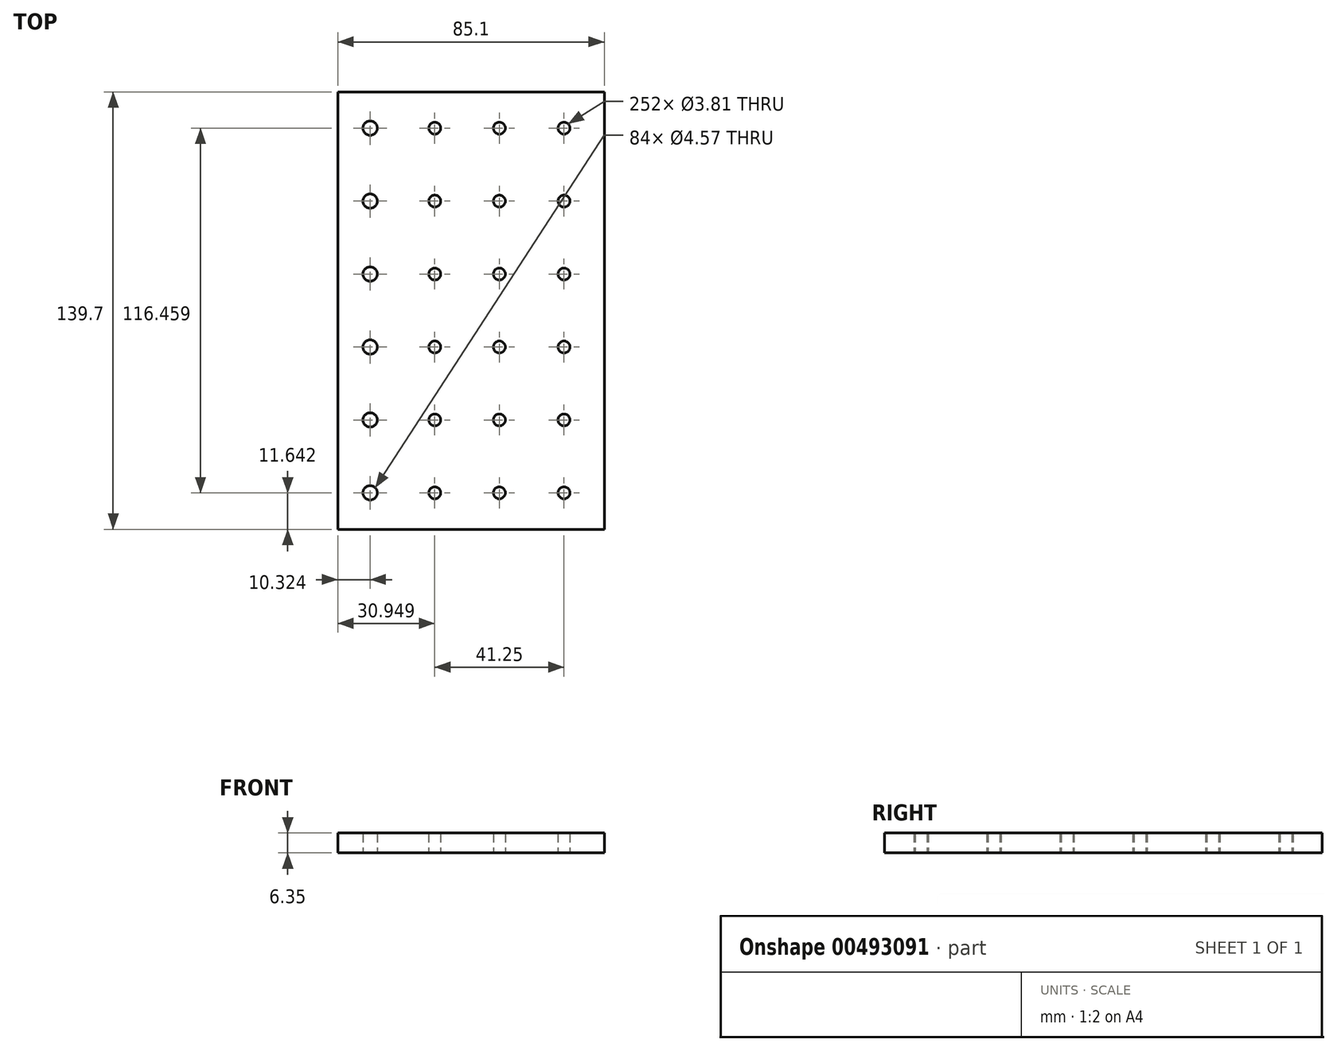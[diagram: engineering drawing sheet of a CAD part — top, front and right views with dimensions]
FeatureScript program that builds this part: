
annotation { "Feature Type Name" : "Feature", "Feature Type Description" : "" }
export const myFeature = defineFeature(function(context is Context, id is Id, definition is map)
    precondition{}
    {
        {
            var Q0;
            Q0=qCreatedBy(makeId("Top.planeOp"),FACE);
            var sketch = newSketch(context, id + "F0", { "sketchPlane" : qUnion([Q0])});
            skLineSegment(sketch, "E0.bottom", {"start": v(-42.54, 69.85) * mm, "end": v(42.55, 69.85) * mm});
            skLineSegment(sketch, "E0.top", {"start": v(-42.55, -69.85) * mm, "end": v(42.55, -69.85) * mm});
            skLineSegment(sketch, "E0.left", {"start": v(-42.54, 69.85) * mm, "end": v(-42.55, -69.85) * mm});
            skLineSegment(sketch, "E0.right", {"start": v(42.55, 69.85) * mm, "end": v(42.55, -69.85) * mm});
            skPoint(sketch, "E0.middle", {"position": v(0, 0) * mm});
            skSolve(sketch);
        }
        {
            var Q0;
            Q0 = qSketchRegion(id + "F0", true);
            extrude(context, id + "F1", {"entities" : qUnion([Q0]), "depth" : 6.35 * mm});
        }
        {
            var Q0;
            Q0=qCreatedBy(makeId("Top.planeOp"),FACE);
            var sketch = newSketch(context, id + "F2", { "sketchPlane" : qUnion([Q0])});
            skCircle(sketch, "E1", {"center": v(-32.23, -58.2) * mm, "radius": 1.9 * mm});
            skCircle(sketch, "E2.0.1.0", {"center": v(-32.23, -34.92) * mm, "radius": 1.9 * mm});
            skCircle(sketch, "E2.0.2.0", {"center": v(-32.23, -11.62) * mm, "radius": 1.9 * mm});
            skCircle(sketch, "E2.0.3.0", {"center": v(-32.23, 11.67) * mm, "radius": 1.9 * mm});
            skCircle(sketch, "E2.0.4.0", {"center": v(-32.23, 34.96) * mm, "radius": 1.9 * mm});
            skCircle(sketch, "E2.0.5.0", {"center": v(-32.23, 58.25) * mm, "radius": 1.9 * mm});
            skCircle(sketch, "E2.1.0.0", {"center": v(-11.6, -58.2) * mm, "radius": 1.9 * mm});
            skCircle(sketch, "E2.1.1.0", {"center": v(-11.6, -34.92) * mm, "radius": 1.9 * mm});
            skCircle(sketch, "E2.1.2.0", {"center": v(-11.6, -11.62) * mm, "radius": 1.9 * mm});
            skCircle(sketch, "E2.1.3.0", {"center": v(-11.6, 11.67) * mm, "radius": 1.9 * mm});
            skCircle(sketch, "E2.1.4.0", {"center": v(-11.6, 34.96) * mm, "radius": 1.9 * mm});
            skCircle(sketch, "E2.1.5.0", {"center": v(-11.6, 58.25) * mm, "radius": 1.9 * mm});
            skCircle(sketch, "E2.2.0.0", {"center": v(9.02, -58.2) * mm, "radius": 1.9 * mm});
            skCircle(sketch, "E2.2.1.0", {"center": v(9.02, -34.92) * mm, "radius": 1.9 * mm});
            skCircle(sketch, "E2.2.2.0", {"center": v(9.02, -11.62) * mm, "radius": 1.9 * mm});
            skCircle(sketch, "E2.2.3.0", {"center": v(9.02, 11.67) * mm, "radius": 1.9 * mm});
            skCircle(sketch, "E2.2.4.0", {"center": v(9.02, 34.96) * mm, "radius": 1.9 * mm});
            skCircle(sketch, "E2.2.5.0", {"center": v(9.02, 58.25) * mm, "radius": 1.9 * mm});
            skCircle(sketch, "E2.3.0.0", {"center": v(29.65, -58.2) * mm, "radius": 1.9 * mm});
            skCircle(sketch, "E2.3.1.0", {"center": v(29.65, -34.92) * mm, "radius": 1.9 * mm});
            skCircle(sketch, "E2.3.2.0", {"center": v(29.65, -11.62) * mm, "radius": 1.9 * mm});
            skCircle(sketch, "E2.3.3.0", {"center": v(29.65, 11.67) * mm, "radius": 1.9 * mm});
            skCircle(sketch, "E2.3.4.0", {"center": v(29.65, 34.96) * mm, "radius": 1.9 * mm});
            skCircle(sketch, "E2.3.5.0", {"center": v(29.65, 58.25) * mm, "radius": 1.9 * mm});
            skLineSegment(sketch, "E2.direction1", {"start": v(-32.23, -58.2) * mm, "end": v(-11.6, -58.2) * mm, "construction": true});
            skLineSegment(sketch, "E2.direction2", {"start": v(-32.23, -58.2) * mm, "end": v(-32.23, -34.92) * mm, "construction": true});
            skSolve(sketch);
        }
        {
            var Q0;
            Q0 = qSketchRegion(id + "F2", true);
            extrude(context, id + "F3", {"entities" : qUnion([Q0]), "operationType" : NewBodyOperationType.REMOVE, "endBound" : BoundingType.THROUGH_ALL, "depth" : 25.4 * mm});
        }
        {
            var Q0;
            Q0=qCreatedBy(makeId("Top.planeOp"),FACE);
            var sketch = newSketch(context, id + "F4", { "sketchPlane" : qUnion([Q0])});
            skCircle(sketch, "E3.0", {"center": v(-32.23, -58.2) * mm, "radius": 1.9 * mm, "construction": true});
            skCircle(sketch, "E4.0", {"center": v(-32.23, -34.92) * mm, "radius": 1.9 * mm, "construction": true});
            skCircle(sketch, "E5.0", {"center": v(-32.23, 11.67) * mm, "radius": 1.9 * mm, "construction": true});
            skCircle(sketch, "E6.0", {"center": v(-32.23, 34.96) * mm, "radius": 1.9 * mm, "construction": true});
            skCircle(sketch, "E7.0", {"center": v(-32.23, 58.25) * mm, "radius": 1.9 * mm, "construction": true});
            skCircle(sketch, "E8.0", {"center": v(-32.23, -11.62) * mm, "radius": 1.9 * mm, "construction": true});
            skCircle(sketch, "E9", {"center": v(-32.23, -58.2) * mm, "radius": 2.29 * mm});
            skCircle(sketch, "E10", {"center": v(-32.23, -34.92) * mm, "radius": 2.29 * mm});
            skCircle(sketch, "E11", {"center": v(-32.23, -11.62) * mm, "radius": 2.29 * mm});
            skCircle(sketch, "E12", {"center": v(-32.23, 11.67) * mm, "radius": 2.29 * mm});
            skCircle(sketch, "E13", {"center": v(-32.23, 34.96) * mm, "radius": 2.29 * mm});
            skCircle(sketch, "E14", {"center": v(-32.23, 58.25) * mm, "radius": 2.29 * mm});
            skSolve(sketch);
        }
        {
            var Q0;
            Q0 = qSketchRegion(id + "F4", true);
            extrude(context, id + "F5", {"entities" : qUnion([Q0]), "operationType" : NewBodyOperationType.REMOVE, "endBound" : BoundingType.THROUGH_ALL, "depth" : 25.4 * mm});
        }
    });
